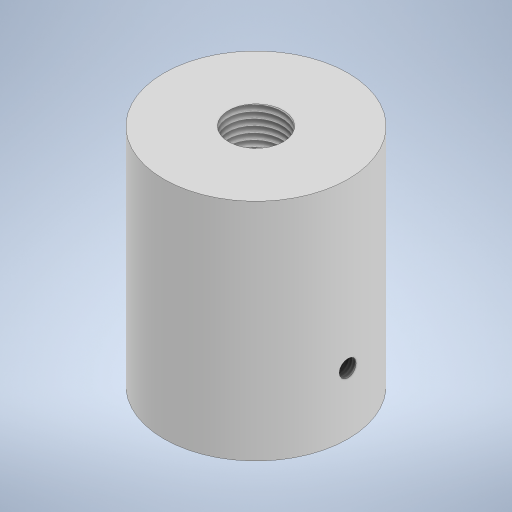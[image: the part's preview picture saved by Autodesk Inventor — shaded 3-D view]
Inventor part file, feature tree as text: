
AUTODESK INVENTOR PART (.ipt)
format: ipt  version: 2023 (Build 270158000, 158)  size: 232,960 bytes
history: native  units: mm
features: sketch x5, other x2, extrude x2, hole x2
ambient origin geometry x8: Origin, YZ Plane, XZ Plane, XY Plane, X Axis, Y Axis, Z Axis, Center Point
bodies: Body1 (feature_tree)
feature tree (11):
  other  "Твердое тело1"
  extrude  "Выдавливание1"  Depth=45.0mm
  sketch  "Эскиз2"
  other  "РабПлоскость1"
  hole  "Отверстие1"  [1 undecoded]
  hole  "Отверстие2"  [1 undecoded]
  extrude  "Выдавливание2"  Depth=5.0mm
  sketch  "Эскиз1"
  sketch  "Эскиз3"
  sketch  "Эскиз4"
  sketch  "Эскиз5"
note: 2 required parameter values undecoded (feature->parameter linkage not recoverable at this tier; creation-order binding heuristic only, values carry confidence <= 0.55)
